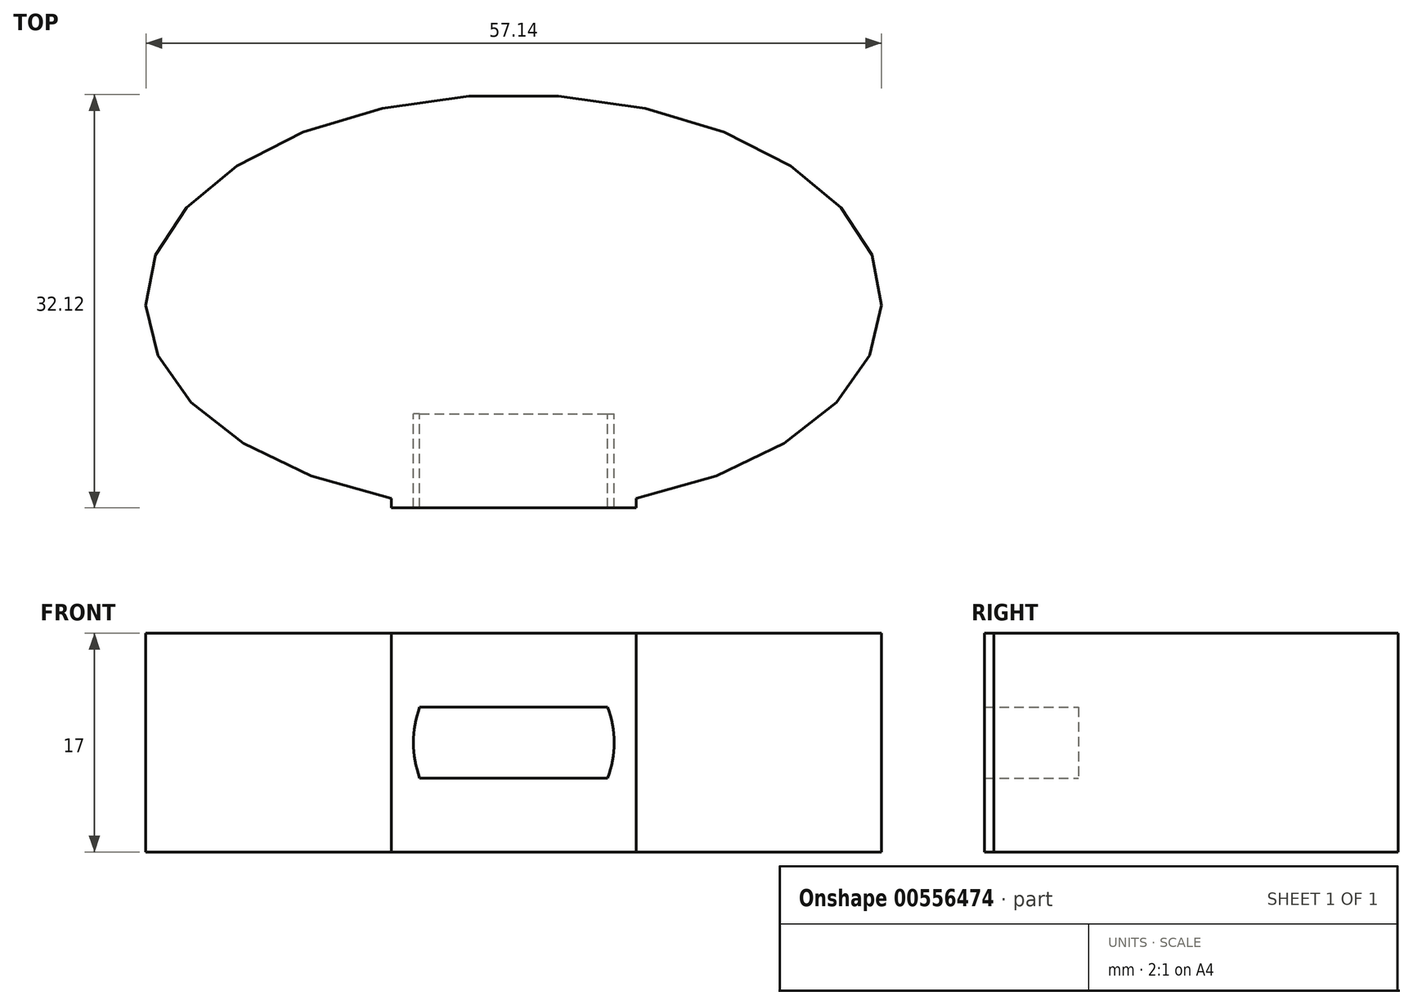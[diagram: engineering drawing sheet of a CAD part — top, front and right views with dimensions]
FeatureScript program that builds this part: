
annotation { "Feature Type Name" : "Feature", "Feature Type Description" : "" }
export const myFeature = defineFeature(function(context is Context, id is Id, definition is map)
    precondition{}
    {
        {
            var Q0;
            Q0=qCreatedBy(makeId("Top.planeOp"),FACE);
            var sketch = newSketch(context, id + "F0", { "sketchPlane" : qUnion([Q0])});
            skEllipse(sketch, "E0", {"center": v(0, 0) * mm, "majorRadius": 28.57 * mm, "minorRadius": 16.16 * mm, "majorAxis": v(1, 0)});
            skLineSegment(sketch, "E1.bottom", {"start": v(-9.5, 0) * mm, "end": v(9.5, 0) * mm});
            skLineSegment(sketch, "E1.top", {"start": v(-9.5, -20.8) * mm, "end": v(9.5, -20.8) * mm});
            skLineSegment(sketch, "E1.left", {"start": v(-9.5, 0) * mm, "end": v(-9.5, -20.8) * mm});
            skLineSegment(sketch, "E1.right", {"start": v(9.5, 0) * mm, "end": v(9.5, -20.8) * mm});
            skLineSegment(sketch, "E2", {"start": v(0, 0) * mm, "end": v(0, -16.16) * mm, "construction": true});
            skSolve(sketch);
        }
        {
            var Q0;
            {var subQ5=sQuery(id+"F0.wireOp",EDGE,"E1.bottom");Q0=makeQuery(id+"F0.imprint","IMPRINT",FACE,{"disambiguationData":[TD([[makeQuery(id+"F0.imprint","IMPRINT",EDGE,{"derivedFrom":subQ5}),1.0]])]});}
            extrude(context, id + "F1", {"entities" : qUnion([Q0]), "depth" : 17 * mm, "offsetDistance" : 25 * mm});
        }
        {
            var Q0;
            Q0=makeQuery(id+"F1.opExtrude","SWEPT_FACE",FACE,{"disambiguationData":[OSD([sQuery(id+"F0.wireOp",EDGE,"E1.bottom")])]});
            cPlane(context, id + "F2", {"entities" : qUnion([Q0]), "cplaneType" : CPlaneType.OFFSET, "offset" : 8.65 * mm, "width" : 150 * mm, "height" : 150 * mm});
        }
        {
            var Q0;
            Q0=qCreatedBy(id+"F2.planeOp",FACE);
            var sketch = newSketch(context, id + "F3", { "sketchPlane" : qUnion([Q0])});
            skLineSegment(sketch, "E3.0", {"start": v(-9.5, 17) * mm, "end": v(9.5, 17) * mm});
            skLineSegment(sketch, "E3.1", {"start": v(-9.5, 0) * mm, "end": v(9.5, 0) * mm});
            skLineSegment(sketch, "E3.2", {"start": v(-9.5, 17) * mm, "end": v(-9.5, 0) * mm});
            skLineSegment(sketch, "E3.3", {"start": v(9.5, 17) * mm, "end": v(9.5, 0) * mm});
            skLineSegment(sketch, "E4", {"start": v(-9.5, 11.25) * mm, "end": v(9.5, 11.25) * mm});
            skLineSegment(sketch, "E5", {"start": v(-9.5, 5.75) * mm, "end": v(9.5, 5.75) * mm});
            skLineSegment(sketch, "E6", {"start": v(-9.5, 17) * mm, "end": v(9.5, 0) * mm, "construction": true});
            skLineSegment(sketch, "E7", {"start": v(-9.5, 0) * mm, "end": v(9.5, 17) * mm, "construction": true});
            skCircle(sketch, "E8", {"center": v(0, 8.5) * mm, "radius": 7.8 * mm});
            skSolve(sketch);
        }
        {
            var Q0;
            {var subQ5=sQuery(id+"F3.wireOp",EDGE,"E3.0");Q0=makeQuery(id+"F3.imprint","IMPRINT",FACE,{"disambiguationData":[TD([[makeQuery(id+"F3.imprint","IMPRINT",EDGE,{"derivedFrom":subQ5}),-1.0]])]});}
            var Q1;
            {var subQ0=sQuery(id+"F3.wireOp",EDGE,"E4");var subQ1=sQuery(id+"F3.wireOp",EDGE,"E3.2");var subQ2=makeQuery(id+"F3.imprint","INTERSECT",VERTEX,{"derivedFrom":[subQ1,subQ0]});Q1=makeQuery(id+"F3.imprint","IMPRINT",FACE,{"disambiguationData":[TD([[makeQuery(id+"F3.imprint","IMPRINT",EDGE,{"disambiguationData":[TD([[subQ2,-1.0]])],"derivedFrom":subQ1}),1.0]])]});}
            var Q2;
            {var subQ1=sQuery(id+"F3.wireOp",EDGE,"E3.1");Q2=makeQuery(id+"F3.imprint","IMPRINT",FACE,{"disambiguationData":[TD([[makeQuery(id+"F3.imprint","IMPRINT",EDGE,{"derivedFrom":subQ1}),1.0]])]});}
            var Q3;
            {var subQ0=sQuery(id+"F3.wireOp",EDGE,"E8");var subQ1=sQuery(id+"F3.wireOp",EDGE,"E5");var subQ2=makeQuery(id+"F3.imprint","INTERSECT",VERTEX,{"disambiguationData":[OD(0.0)],"derivedFrom":[subQ1,subQ0]});Q3=makeQuery(id+"F3.imprint","IMPRINT",FACE,{"disambiguationData":[TD([[makeQuery(id+"F3.imprint","IMPRINT",EDGE,{"disambiguationData":[TD([[subQ2,-1.0]])],"derivedFrom":subQ1}),-1.0]])]});}
            var Q4;
            {var subQ0=sQuery(id+"F3.wireOp",EDGE,"E8");var subQ1=sQuery(id+"F3.wireOp",EDGE,"E4");var subQ2=makeQuery(id+"F3.imprint","INTERSECT",VERTEX,{"disambiguationData":[OD(0.0)],"derivedFrom":[subQ1,subQ0]});Q4=makeQuery(id+"F3.imprint","IMPRINT",FACE,{"disambiguationData":[TD([[makeQuery(id+"F3.imprint","IMPRINT",EDGE,{"disambiguationData":[TD([[subQ2,-1.0]])],"derivedFrom":subQ1}),1.0]])]});}
            var Q5;
            {var subQ0=sQuery(id+"F3.wireOp",EDGE,"E4");var subQ1=sQuery(id+"F3.wireOp",EDGE,"E3.3");var subQ2=makeQuery(id+"F3.imprint","INTERSECT",VERTEX,{"derivedFrom":[subQ1,subQ0]});Q5=makeQuery(id+"F3.imprint","IMPRINT",FACE,{"disambiguationData":[TD([[makeQuery(id+"F3.imprint","IMPRINT",EDGE,{"disambiguationData":[TD([[subQ2,-1.0]])],"derivedFrom":subQ1}),-1.0]])]});}
            extrude(context, id + "F4", {"entities" : qUnion([Q0, Q1, Q2, Q3, Q4, Q5]), "operationType" : NewBodyOperationType.ADD, "depth" : 7.3 * mm, "offsetDistance" : 25 * mm});
        }
        {
            var Q0;
            {var subQ5=sQuery(id+"F3.wireOp",EDGE,"E3.0");Q0=makeQuery(id+"F3.imprint","IMPRINT",FACE,{"disambiguationData":[TD([[makeQuery(id+"F3.imprint","IMPRINT",EDGE,{"derivedFrom":subQ5}),-1.0]])]});}
            var Q1;
            {var subQ0=sQuery(id+"F3.wireOp",EDGE,"E8");var subQ1=sQuery(id+"F3.wireOp",EDGE,"E4");var subQ2=makeQuery(id+"F3.imprint","INTERSECT",VERTEX,{"disambiguationData":[OD(0.0)],"derivedFrom":[subQ1,subQ0]});Q1=makeQuery(id+"F3.imprint","IMPRINT",FACE,{"disambiguationData":[TD([[makeQuery(id+"F3.imprint","IMPRINT",EDGE,{"disambiguationData":[TD([[subQ2,-1.0]])],"derivedFrom":subQ1}),1.0]])]});}
            var Q2;
            {var subQ0=sQuery(id+"F3.wireOp",EDGE,"E8");var subQ1=sQuery(id+"F3.wireOp",EDGE,"E4");var subQ2=makeQuery(id+"F3.imprint","INTERSECT",VERTEX,{"disambiguationData":[OD(0.0)],"derivedFrom":[subQ1,subQ0]});Q2=makeQuery(id+"F3.imprint","IMPRINT",FACE,{"disambiguationData":[TD([[makeQuery(id+"F3.imprint","IMPRINT",EDGE,{"disambiguationData":[TD([[subQ2,-1.0]])],"derivedFrom":subQ1}),-1.0]])]});}
            var Q3;
            {var subQ0=sQuery(id+"F3.wireOp",EDGE,"E4");var subQ1=sQuery(id+"F3.wireOp",EDGE,"E3.2");var subQ2=makeQuery(id+"F3.imprint","INTERSECT",VERTEX,{"derivedFrom":[subQ1,subQ0]});Q3=makeQuery(id+"F3.imprint","IMPRINT",FACE,{"disambiguationData":[TD([[makeQuery(id+"F3.imprint","IMPRINT",EDGE,{"disambiguationData":[TD([[subQ2,-1.0]])],"derivedFrom":subQ1}),1.0]])]});}
            var Q4;
            {var subQ1=sQuery(id+"F3.wireOp",EDGE,"E3.1");Q4=makeQuery(id+"F3.imprint","IMPRINT",FACE,{"disambiguationData":[TD([[makeQuery(id+"F3.imprint","IMPRINT",EDGE,{"derivedFrom":subQ1}),1.0]])]});}
            var Q5;
            {var subQ0=sQuery(id+"F3.wireOp",EDGE,"E8");var subQ1=sQuery(id+"F3.wireOp",EDGE,"E5");var subQ2=makeQuery(id+"F3.imprint","INTERSECT",VERTEX,{"disambiguationData":[OD(0.0)],"derivedFrom":[subQ1,subQ0]});Q5=makeQuery(id+"F3.imprint","IMPRINT",FACE,{"disambiguationData":[TD([[makeQuery(id+"F3.imprint","IMPRINT",EDGE,{"disambiguationData":[TD([[subQ2,-1.0]])],"derivedFrom":subQ1}),-1.0]])]});}
            var Q6;
            {var subQ0=sQuery(id+"F3.wireOp",EDGE,"E4");var subQ1=sQuery(id+"F3.wireOp",EDGE,"E3.3");var subQ2=makeQuery(id+"F3.imprint","INTERSECT",VERTEX,{"derivedFrom":[subQ1,subQ0]});Q6=makeQuery(id+"F3.imprint","IMPRINT",FACE,{"disambiguationData":[TD([[makeQuery(id+"F3.imprint","IMPRINT",EDGE,{"disambiguationData":[TD([[subQ2,-1.0]])],"derivedFrom":subQ1}),-1.0]])]});}
            var Q7;
            Q7=makeQuery(id+"F1.opExtrude","SWEPT_FACE",FACE,{"disambiguationData":[OSD([sQuery(id+"F0.wireOp",EDGE,"E1.bottom")])]});
            extrude(context, id + "F5", {"entities" : qUnion([Q0, Q1, Q2, Q3, Q4, Q5, Q6]), "operationType" : NewBodyOperationType.ADD, "endBound" : BoundingType.UP_TO_SURFACE, "oppositeDirection" : true, "depth" : 25 * mm, "endBoundEntityFace" : qUnion([Q7]), "offsetDistance" : 25 * mm});
        }
    });
